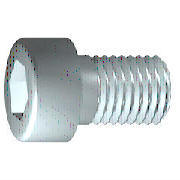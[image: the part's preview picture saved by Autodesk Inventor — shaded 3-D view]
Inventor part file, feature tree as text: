
AUTODESK INVENTOR PART (.ipt)
format: ipt  version: 2013 (Build 170138000, 138)  size: 182,272 bytes
history: native  units: mm (DEFAULTED — no unit token found)
features: sketch x2, extrude x1, plane x1, fillet x1
ambient origin geometry x7: Origin, YZ Plane, XY Plane, X Axis, Y Axis, Z Axis, Center Point
bodies: Solid1 (feature_tree), Body (feature_tree)
feature tree (5):
  extrude  "Slot"  Depth=0.306825mm
  plane  "Work Plane1"
  fillet  "Fillet2"  Radius=3.0mm
  sketch  "Sketch1"  dims[d1=18.0mm d2=0.306825mm d3=3.0mm]
  sketch  "Sketch2"  dims[d4=1.5mm d5=60.0deg d6=3.0mm d7=3.0mm d8=2.886751mm d9=5.5mm d10=90.0deg d11=10.0mm d12=0.0mm d13=18.0mm d14=0.0mm d15=0.306725mm d16=0.306725mm d17=0.3mm d19=0.0mm d26=45.0mm d27=45.0deg d28=0.0mm d29=0.0mm d30=0.1mm]
